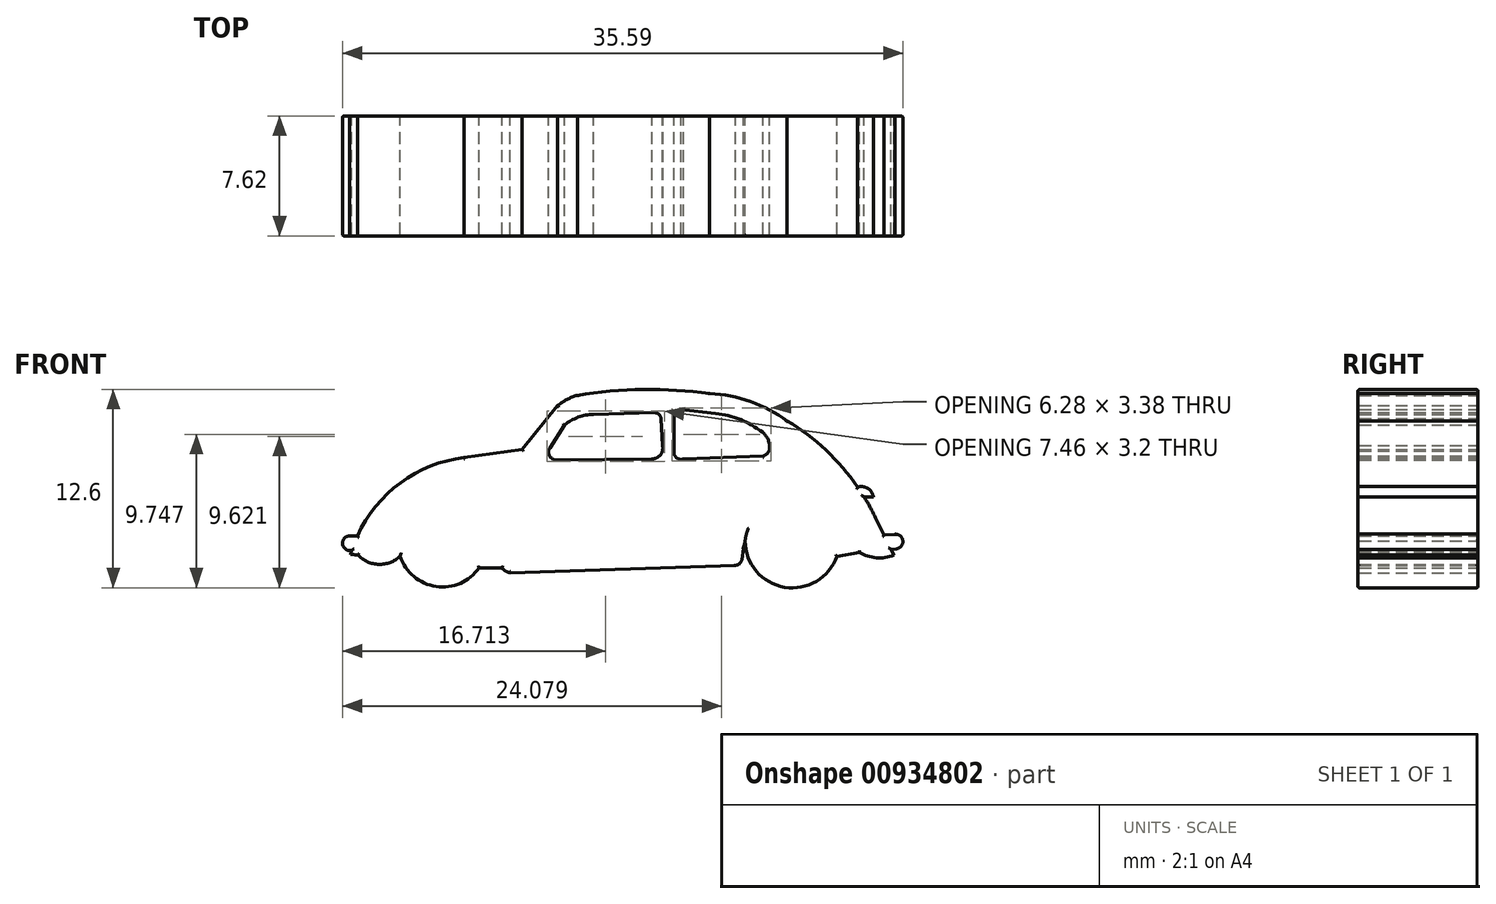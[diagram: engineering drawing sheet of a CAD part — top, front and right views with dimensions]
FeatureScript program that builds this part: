
annotation { "Feature Type Name" : "Feature", "Feature Type Description" : "" }
export const myFeature = defineFeature(function(context is Context, id is Id, definition is map)
    precondition{}
    {
        {
            var Q0;
            Q0=qCreatedBy(makeId("Front.planeOp"),FACE);
            var sketch = newSketch(context, id + "F0", { "sketchPlane" : qUnion([Q0])});
            skArc(sketch, "E0", {"start": v(-11.53, 23.27) * mm, "mid": v(-15.57, 21.68) * mm, "end": v(-18.3, 18.3) * mm});
            skArc(sketch, "E1", {"start": v(8.99, 25.61) * mm, "mid": v(6.65, 26.83) * mm, "end": v(4.07, 27.35) * mm});
            skArc(sketch, "E2", {"start": v(-15.59, 17) * mm, "mid": v(-13.3, 15.08) * mm, "end": v(-10.57, 16.27) * mm});
            skArc(sketch, "E3", {"start": v(6.32, 17.98) * mm, "mid": v(8.82, 15.04) * mm, "end": v(12.15, 17) * mm});
            skPoint(sketch, "E4.first.point", {"position": v(-9.3, 16.64) * mm});
            skPoint(sketch, "E4.second.point", {"position": v(-16.14, 17.08) * mm});
            skPoint(sketch, "E4.third.point", {"position": v(-15.9, 15.72) * mm});
            skPoint(sketch, "E5.first.point", {"position": v(6.84, 18.84) * mm});
            skPoint(sketch, "E5.second.point", {"position": v(12.55, 16.03) * mm});
            skPoint(sketch, "E5.third.point", {"position": v(9.32, 20.48) * mm});
            skLineSegment(sketch, "E6", {"start": v(-7.85, 23.8) * mm, "end": v(-5.6, 26.57) * mm});
            skLineSegment(sketch, "E7", {"start": v(-7.85, 23.8) * mm, "end": v(-11.53, 23.27) * mm});
            skPoint(sketch, "E8.second.point", {"position": v(-0.88, 20.92) * mm});
            skPoint(sketch, "E8.third.point", {"position": v(0.26, 22.68) * mm});
            skPoint(sketch, "E9.first.point", {"position": v(12.94, 17.76) * mm});
            skPoint(sketch, "E9.second.point", {"position": v(14.7, 18.65) * mm});
            skPoint(sketch, "E9.third.point", {"position": v(14.48, 18.97) * mm});
            skPoint(sketch, "E10.first.point", {"position": v(12.5, 18.64) * mm});
            skPoint(sketch, "E10.second.point", {"position": v(16.16, 21.44) * mm});
            skPoint(sketch, "E10.third.point", {"position": v(16.02, 21.52) * mm});
            skPoint(sketch, "E11.first.point", {"position": v(11.44, 23.75) * mm});
            skArc(sketch, "E12", {"start": v(-18.74, 17.14) * mm, "mid": v(-18.5, 17.1) * mm, "end": v(-18.27, 17.1) * mm});
            skPoint(sketch, "E12.first.point", {"position": v(-15.9, 18.25) * mm});
            skPoint(sketch, "E12.second.point", {"position": v(-20.76, 21.48) * mm});
            skPoint(sketch, "E12.third.point", {"position": v(-20.1, 17.77) * mm});
            skArc(sketch, "E13", {"start": v(-9.13, 16.27) * mm, "mid": v(-8.75, 16) * mm, "end": v(-8.27, 15.97) * mm});
            skPoint(sketch, "E13.second.point", {"position": v(-7.64, 17.02) * mm});
            skPoint(sketch, "E13.third.point", {"position": v(-8.6, 15.96) * mm});
            skLineSegment(sketch, "E14.trimOffspring", {"start": v(-8.6, 15.96) * mm, "end": v(-8.27, 15.97) * mm});
            skArc(sketch, "E15.trimOffspring", {"start": v(-4.34, 27.23) * mm, "mid": v(-5, 26.96) * mm, "end": v(-5.6, 26.57) * mm});
            skArc(sketch, "E16.trimOffspring", {"start": v(16.16, 21.44) * mm, "mid": v(16.09, 21.48) * mm, "end": v(16.02, 21.52) * mm});
            skArc(sketch, "E17.trimOffspring", {"start": v(14.61, 19.44) * mm, "mid": v(14.26, 20.12) * mm, "end": v(13.88, 20.77) * mm});
            skPoint(sketch, "E18.first.point", {"position": v(-9.43, 17.2) * mm});
            skPoint(sketch, "E18.second.point", {"position": v(-16.83, 16.34) * mm});
            skPoint(sketch, "E18.third.point", {"position": v(-14.78, 13.44) * mm});
            skArc(sketch, "E19", {"start": v(4.07, 27.35) * mm, "mid": v(-0.14, 27.6) * mm, "end": v(-4.34, 27.23) * mm});
            skPoint(sketch, "E20.end.orphan", {"position": v(4.07, 27.35) * mm});
            skArc(sketch, "E21", {"start": v(14.46, 20.77) * mm, "mid": v(14.1, 21.32) * mm, "end": v(13.47, 21.4) * mm});
            skPoint(sketch, "E21.first.point", {"position": v(13.47, 21.4) * mm});
            skPoint(sketch, "E21.second.point", {"position": v(13.78, 19.9) * mm});
            skPoint(sketch, "E21.third.point", {"position": v(14.26, 20.13) * mm});
            skLineSegment(sketch, "E22", {"start": v(14.46, 20.77) * mm, "end": v(13.88, 20.77) * mm});
            skArc(sketch, "E23.trimOffspring", {"start": v(13.47, 21.4) * mm, "mid": v(11.45, 23.74) * mm, "end": v(8.99, 25.61) * mm});
            skLineSegment(sketch, "E24", {"start": v(14.61, 19.44) * mm, "end": v(15.14, 18.36) * mm});
            skArc(sketch, "E25", {"start": v(15.9, 17.47) * mm, "mid": v(16.34, 17.97) * mm, "end": v(15.83, 18.4) * mm});
            skLineSegment(sketch, "E26", {"start": v(15.9, 17.47) * mm, "end": v(15.59, 17.45) * mm});
            skLineSegment(sketch, "E27", {"start": v(15.83, 18.4) * mm, "end": v(15.14, 18.36) * mm});
            skPoint(sketch, "E27.endSnap0", {"position": v(15.2, 18.26) * mm});
            skPoint(sketch, "E28.orphan", {"position": v(15.2, 18.36) * mm});
            skArc(sketch, "E29", {"start": v(-18.76, 18.3) * mm, "mid": v(-19.25, 17.87) * mm, "end": v(-18.83, 17.37) * mm});
            skArc(sketch, "E30.trimOffspring", {"start": v(-18.67, 17.37) * mm, "mid": v(-18.7, 17.25) * mm, "end": v(-18.74, 17.14) * mm});
            skLineSegment(sketch, "E31", {"start": v(-18.8, 18.3) * mm, "end": v(-18.3, 18.3) * mm});
            skLineSegment(sketch, "E32", {"start": v(-18.83, 17.37) * mm, "end": v(-18.67, 17.37) * mm});
            skPoint(sketch, "E33.orphan", {"position": v(-18.3, 17.38) * mm});
            skPoint(sketch, "E34.orphan", {"position": v(-18.66, 17.38) * mm});
            skLineSegment(sketch, "E35.trimOffspring", {"start": v(15.59, 17.45) * mm, "end": v(15.77, 17.08) * mm});
            skPoint(sketch, "E36.first.point", {"position": v(7.3, 19.61) * mm});
            skPoint(sketch, "E36.second.point", {"position": v(11.9, 14.6) * mm});
            skPoint(sketch, "E36.third.point", {"position": v(12.82, 16.03) * mm});
            skArc(sketch, "E37", {"start": v(5.67, 16.42) * mm, "mid": v(5.96, 16.53) * mm, "end": v(6.12, 16.8) * mm});
            skPoint(sketch, "E37.first.point", {"position": v(6.12, 16.93) * mm});
            skPoint(sketch, "E37.second.point", {"position": v(5.22, 16.82) * mm});
            skPoint(sketch, "E37.third.point", {"position": v(5.67, 16.42) * mm});
            skLineSegment(sketch, "E38", {"start": v(6.23, 17.51) * mm, "end": v(6.12, 16.8) * mm});
            skArc(sketch, "E39.trimOffspring", {"start": v(6.32, 17.98) * mm, "mid": v(6.27, 17.75) * mm, "end": v(6.23, 17.51) * mm});
            skPoint(sketch, "E40.first.point", {"position": v(0.33, 26.04) * mm});
            skPoint(sketch, "E40.second.point", {"position": v(0.73, 25.33) * mm});
            skPoint(sketch, "E40.third.point", {"position": v(0.53, 25.3) * mm});
            skArc(sketch, "E41", {"start": v(0.4, 23.19) * mm, "mid": v(0.94, 23.44) * mm, "end": v(1.07, 24.03) * mm});
            skPoint(sketch, "E41.first.point", {"position": v(1.07, 23.71) * mm});
            skPoint(sketch, "E41.second.point", {"position": v(-0.24, 24.08) * mm});
            skPoint(sketch, "E41.third.point", {"position": v(0.4, 23.19) * mm});
            skArc(sketch, "E42", {"start": v(-6.05, 23.94) * mm, "mid": v(-6.11, 23.4) * mm, "end": v(-5.64, 23.12) * mm});
            skPoint(sketch, "E42.first.point", {"position": v(-5.92, 23.19) * mm});
            skPoint(sketch, "E42.second.point", {"position": v(-5.35, 24) * mm});
            skPoint(sketch, "E42.third.point", {"position": v(-5.6, 24.12) * mm});
            skArc(sketch, "E43", {"start": v(-3.31, 26.01) * mm, "mid": v(-4.29, 25.83) * mm, "end": v(-5.15, 25.33) * mm});
            skPoint(sketch, "E43.first.point", {"position": v(-5.15, 25.33) * mm});
            skPoint(sketch, "E43.second.point", {"position": v(-1.4, 21) * mm});
            skPoint(sketch, "E43.third.point", {"position": v(-0.47, 23.64) * mm});
            skLineSegment(sketch, "E44", {"start": v(-5.15, 25.33) * mm, "end": v(-6.08, 23.9) * mm});
            skLineSegment(sketch, "E45", {"start": v(-3.31, 26.01) * mm, "end": v(0.56, 26.12) * mm});
            skLineSegment(sketch, "E46", {"start": v(-5.64, 23.12) * mm, "end": v(0.4, 23.19) * mm});
            skLineSegment(sketch, "E47", {"start": v(1.07, 24.03) * mm, "end": v(0.98, 25.73) * mm});
            skArc(sketch, "E48.trimOffspring", {"start": v(0.98, 25.73) * mm, "mid": v(0.75, 26.08) * mm, "end": v(0.33, 26.04) * mm});
            skArc(sketch, "E49.trimOffspring", {"start": v(-6.05, 23.95) * mm, "mid": v(-6.05, 23.95) * mm, "end": v(-6.05, 23.94) * mm});
            skArc(sketch, "E50", {"start": v(2.25, 26.33) * mm, "mid": v(1.9, 26.13) * mm, "end": v(1.79, 25.75) * mm});
            skPoint(sketch, "E50.first.point", {"position": v(1.79, 25.85) * mm});
            skPoint(sketch, "E50.second.point", {"position": v(2.85, 25.68) * mm});
            skPoint(sketch, "E50.third.point", {"position": v(2.05, 25.34) * mm});
            skArc(sketch, "E51", {"start": v(1.8, 23.68) * mm, "mid": v(1.96, 23.26) * mm, "end": v(2.41, 23.19) * mm});
            skPoint(sketch, "E51.first.point", {"position": v(1.8, 23.68) * mm});
            skPoint(sketch, "E51.second.point", {"position": v(2.7, 23.57) * mm});
            skPoint(sketch, "E51.third.point", {"position": v(2.7, 23.72) * mm});
            skPoint(sketch, "E52.first.point", {"position": v(7.78, 23.5) * mm});
            skPoint(sketch, "E52.second.point", {"position": v(5.63, 24.43) * mm});
            skPoint(sketch, "E52.third.point", {"position": v(5.78, 23.24) * mm});
            skArc(sketch, "E53", {"start": v(1.79, 25.8) * mm, "mid": v(1.79, 25.8) * mm, "end": v(1.79, 25.8) * mm});
            skPoint(sketch, "E53.first.point", {"position": v(7.41, 24.88) * mm});
            skPoint(sketch, "E53.second.point", {"position": v(-0.05, 15.42) * mm});
            skPoint(sketch, "E53.third.point", {"position": v(3.06, 26.08) * mm});
            skArc(sketch, "E54", {"start": v(7.46, 23.38) * mm, "mid": v(7.7, 23.51) * mm, "end": v(7.85, 23.74) * mm});
            skPoint(sketch, "E54.first.point", {"position": v(7.46, 23.38) * mm});
            skPoint(sketch, "E54.second.point", {"position": v(7.16, 24.47) * mm});
            skPoint(sketch, "E54.third.point", {"position": v(7.12, 24.46) * mm});
            skLineSegment(sketch, "E55", {"start": v(2.41, 23.19) * mm, "end": v(7.46, 23.38) * mm});
            skLineSegment(sketch, "E56", {"start": v(2.25, 26.33) * mm, "end": v(4.45, 26.08) * mm});
            skLineSegment(sketch, "E57", {"start": v(1.79, 25.85) * mm, "end": v(1.8, 23.68) * mm});
            skArc(sketch, "E58.trimOffspring", {"start": v(7.85, 23.74) * mm, "mid": v(7.8, 24.38) * mm, "end": v(7.41, 24.88) * mm});
            skArc(sketch, "E59.trimOffspring", {"start": v(7.41, 24.88) * mm, "mid": v(6, 25.68) * mm, "end": v(4.45, 26.08) * mm});
            skPoint(sketch, "E60.first.point", {"position": v(-17.23, 16.52) * mm});
            skPoint(sketch, "E60.second.point", {"position": v(-16.33, 20.19) * mm});
            skPoint(sketch, "E60.third.point", {"position": v(-16.6, 20.25) * mm});
            skArc(sketch, "E61.trimOffspring", {"start": v(-18.27, 17.1) * mm, "mid": v(-16.95, 16.5) * mm, "end": v(-15.59, 17) * mm});
            skLineSegment(sketch, "E62", {"start": v(-10.57, 16.27) * mm, "end": v(-9.13, 16.27) * mm});
            skLineSegment(sketch, "E63", {"start": v(12.15, 17) * mm, "end": v(13.57, 17.26) * mm});
            skArc(sketch, "E64.trimOffspring", {"start": v(13.57, 17.26) * mm, "mid": v(14.65, 16.9) * mm, "end": v(15.77, 17.08) * mm});
            skPoint(sketch, "E65.1.36", {"position": v(-25.13, -61.05) * mm});
            skPoint(sketch, "E66", {"position": v(-1.45, 16.2) * mm});
            skLineSegment(sketch, "E67", {"start": v(-8.6, 15.96) * mm, "end": v(5.7, 16.43) * mm});
            skPoint(sketch, "E68", {"position": v(-5.03, 16.07) * mm});
            skPoint(sketch, "E69", {"position": v(2.12, 16.3) * mm});
            skSolve(sketch);
        }
        {
            var Q0;
            {var subQ37=sQuery(id+"F0.wireOp",EDGE,"E0");Q0=makeQuery(id+"F0.imprint","IMPRINT",FACE,{"disambiguationData":[TD([[makeQuery(id+"F0.imprint","IMPRINT",EDGE,{"derivedFrom":subQ37}),1.0]])]});}
            extrude(context, id + "F1", {"entities" : qUnion([Q0]), "depth" : 7.62 * mm, "offsetDistance" : 25 * mm});
        }
        {
            var Q0;
            Q0=makeQuery(id+"F1.opExtrude","CAP_FACE",FACE,{"disambiguationData":[OSD([sQuery(id+"F0.wireOp",EDGE,"E0"),sQuery(id+"F0.wireOp",EDGE,"E1"),sQuery(id+"F0.wireOp",EDGE,"E2"),sQuery(id+"F0.wireOp",EDGE,"E3"),sQuery(id+"F0.wireOp",EDGE,"E6"),sQuery(id+"F0.wireOp",EDGE,"E7"),sQuery(id+"F0.wireOp",EDGE,"E12"),sQuery(id+"F0.wireOp",EDGE,"E13"),sQuery(id+"F0.wireOp",EDGE,"E15.trimOffspring"),sQuery(id+"F0.wireOp",EDGE,"E17.trimOffspring"),sQuery(id+"F0.wireOp",EDGE,"E19"),sQuery(id+"F0.wireOp",EDGE,"E21"),sQuery(id+"F0.wireOp",EDGE,"E22"),sQuery(id+"F0.wireOp",EDGE,"E23.trimOffspring"),sQuery(id+"F0.wireOp",EDGE,"E24"),sQuery(id+"F0.wireOp",EDGE,"E25"),sQuery(id+"F0.wireOp",EDGE,"E26"),sQuery(id+"F0.wireOp",EDGE,"E27"),sQuery(id+"F0.wireOp",EDGE,"E29"),sQuery(id+"F0.wireOp",EDGE,"E30.trimOffspring"),sQuery(id+"F0.wireOp",EDGE,"E31"),sQuery(id+"F0.wireOp",EDGE,"E32"),sQuery(id+"F0.wireOp",EDGE,"E35.trimOffspring"),sQuery(id+"F0.wireOp",EDGE,"E37"),sQuery(id+"F0.wireOp",EDGE,"E38"),sQuery(id+"F0.wireOp",EDGE,"E39.trimOffspring"),sQuery(id+"F0.wireOp",EDGE,"E41"),sQuery(id+"F0.wireOp",EDGE,"E42"),sQuery(id+"F0.wireOp",EDGE,"E43"),sQuery(id+"F0.wireOp",EDGE,"E44"),sQuery(id+"F0.wireOp",EDGE,"E45"),sQuery(id+"F0.wireOp",EDGE,"E46"),sQuery(id+"F0.wireOp",EDGE,"E47"),sQuery(id+"F0.wireOp",EDGE,"E48.trimOffspring"),sQuery(id+"F0.wireOp",EDGE,"E50"),sQuery(id+"F0.wireOp",EDGE,"E51"),sQuery(id+"F0.wireOp",EDGE,"E54"),sQuery(id+"F0.wireOp",EDGE,"E55"),sQuery(id+"F0.wireOp",EDGE,"E56"),sQuery(id+"F0.wireOp",EDGE,"E57"),sQuery(id+"F0.wireOp",EDGE,"E58.trimOffspring"),sQuery(id+"F0.wireOp",EDGE,"E59.trimOffspring"),sQuery(id+"F0.wireOp",EDGE,"E61.trimOffspring"),sQuery(id+"F0.wireOp",EDGE,"E62"),sQuery(id+"F0.wireOp",EDGE,"E63"),sQuery(id+"F0.wireOp",EDGE,"E64.trimOffspring"),sQuery(id+"F0.wireOp",EDGE,"E65.1.40"),sQuery(id+"F0.wireOp",EDGE,"E65.1.43"),sQuery(id+"F0.wireOp",EDGE,"E65.1.65"),sQuery(id+"F0.wireOp",EDGE,"E65.1.67"),sQuery(id+"F0.wireOp",EDGE,"E65.1.70"),sQuery(id+"F0.wireOp",EDGE,"E65.1.75"),sQuery(id+"F0.wireOp",EDGE,"E65.1.76"),sQuery(id+"F0.wireOp",EDGE,"E65.1.77"),sQuery(id+"F0.wireOp",EDGE,"E65.1.78"),sQuery(id+"F0.wireOp",EDGE,"E65.1.79"),sQuery(id+"F0.wireOp",EDGE,"E65.1.80"),sQuery(id+"F0.wireOp",EDGE,"E65.1.81"),sQuery(id+"F0.wireOp",EDGE,"E65.1.82"),sQuery(id+"F0.wireOp",EDGE,"E65.1.84"),sQuery(id+"F0.wireOp",EDGE,"E65.1.85"),sQuery(id+"F0.wireOp",EDGE,"E65.1.86"),sQuery(id+"F0.wireOp",EDGE,"E65.1.87"),sQuery(id+"F0.wireOp",EDGE,"E65.1.88"),sQuery(id+"F0.wireOp",EDGE,"E65.1.89"),sQuery(id+"F0.wireOp",EDGE,"E65.1.90"),sQuery(id+"F0.wireOp",EDGE,"E65.1.91"),sQuery(id+"F0.wireOp",EDGE,"E65.1.92"),sQuery(id+"F0.wireOp",EDGE,"E65.1.93"),sQuery(id+"F0.wireOp",EDGE,"E65.1.94"),sQuery(id+"F0.wireOp",EDGE,"E65.1.95"),sQuery(id+"F0.wireOp",EDGE,"E65.1.96"),sQuery(id+"F0.wireOp",EDGE,"E65.1.97"),sQuery(id+"F0.wireOp",EDGE,"E65.1.99"),sQuery(id+"F0.wireOp",EDGE,"E65.1.100"),sQuery(id+"F0.wireOp",EDGE,"E65.1.101"),sQuery(id+"F0.wireOp",EDGE,"E65.1.102"),sQuery(id+"F0.wireOp",EDGE,"E65.1.103"),sQuery(id+"F0.wireOp",EDGE,"E65.1.105"),sQuery(id+"F0.wireOp",EDGE,"E65.1.106"),sQuery(id+"F0.wireOp",EDGE,"E65.1.107"),sQuery(id+"F0.wireOp",EDGE,"E65.1.108"),sQuery(id+"F0.wireOp",EDGE,"E65.1.109"),sQuery(id+"F0.wireOp",EDGE,"E65.1.110"),sQuery(id+"F0.wireOp",EDGE,"E65.1.111"),sQuery(id+"F0.wireOp",EDGE,"E65.1.112"),sQuery(id+"F0.wireOp",EDGE,"E65.1.113"),sQuery(id+"F0.wireOp",EDGE,"E65.1.114"),sQuery(id+"F0.wireOp",EDGE,"E65.1.116"),sQuery(id+"F0.wireOp",EDGE,"E65.1.117"),sQuery(id+"F0.wireOp",EDGE,"E65.1.118"),sQuery(id+"F0.wireOp",EDGE,"E65.1.119"),sQuery(id+"F0.wireOp",EDGE,"E65.1.120"),sQuery(id+"F0.wireOp",EDGE,"E65.2.40"),sQuery(id+"F0.wireOp",EDGE,"E65.2.43"),sQuery(id+"F0.wireOp",EDGE,"E65.2.65"),sQuery(id+"F0.wireOp",EDGE,"E65.2.67"),sQuery(id+"F0.wireOp",EDGE,"E65.2.70"),sQuery(id+"F0.wireOp",EDGE,"E65.2.75"),sQuery(id+"F0.wireOp",EDGE,"E65.2.76"),sQuery(id+"F0.wireOp",EDGE,"E65.2.77"),sQuery(id+"F0.wireOp",EDGE,"E65.2.78"),sQuery(id+"F0.wireOp",EDGE,"E65.2.79"),sQuery(id+"F0.wireOp",EDGE,"E65.2.80"),sQuery(id+"F0.wireOp",EDGE,"E65.2.81"),sQuery(id+"F0.wireOp",EDGE,"E65.2.82"),sQuery(id+"F0.wireOp",EDGE,"E65.2.84"),sQuery(id+"F0.wireOp",EDGE,"E65.2.85"),sQuery(id+"F0.wireOp",EDGE,"E65.2.86"),sQuery(id+"F0.wireOp",EDGE,"E65.2.87"),sQuery(id+"F0.wireOp",EDGE,"E65.2.88"),sQuery(id+"F0.wireOp",EDGE,"E65.2.89"),sQuery(id+"F0.wireOp",EDGE,"E65.2.90"),sQuery(id+"F0.wireOp",EDGE,"E65.2.91"),sQuery(id+"F0.wireOp",EDGE,"E65.2.92"),sQuery(id+"F0.wireOp",EDGE,"E65.2.93"),sQuery(id+"F0.wireOp",EDGE,"E65.2.94"),sQuery(id+"F0.wireOp",EDGE,"E65.2.95"),sQuery(id+"F0.wireOp",EDGE,"E65.2.96"),sQuery(id+"F0.wireOp",EDGE,"E65.2.97"),sQuery(id+"F0.wireOp",EDGE,"E65.2.99"),sQuery(id+"F0.wireOp",EDGE,"E65.2.100"),sQuery(id+"F0.wireOp",EDGE,"E65.2.101"),sQuery(id+"F0.wireOp",EDGE,"E65.2.102"),sQuery(id+"F0.wireOp",EDGE,"E65.2.103"),sQuery(id+"F0.wireOp",EDGE,"E65.2.105"),sQuery(id+"F0.wireOp",EDGE,"E65.2.106"),sQuery(id+"F0.wireOp",EDGE,"E65.2.107"),sQuery(id+"F0.wireOp",EDGE,"E65.2.108"),sQuery(id+"F0.wireOp",EDGE,"E65.2.109"),sQuery(id+"F0.wireOp",EDGE,"E65.2.110"),sQuery(id+"F0.wireOp",EDGE,"E65.2.111"),sQuery(id+"F0.wireOp",EDGE,"E65.2.112"),sQuery(id+"F0.wireOp",EDGE,"E65.2.113"),sQuery(id+"F0.wireOp",EDGE,"E65.2.114"),sQuery(id+"F0.wireOp",EDGE,"E65.2.116"),sQuery(id+"F0.wireOp",EDGE,"E65.2.117"),sQuery(id+"F0.wireOp",EDGE,"E65.2.118"),sQuery(id+"F0.wireOp",EDGE,"E65.2.119"),sQuery(id+"F0.wireOp",EDGE,"E65.2.120"),sQuery(id+"F0.wireOp",EDGE,"cX2E59e6-YhH1-Q1MG-Sjdk-BAABhza4ufgR"),sQuery(id+"F0.wireOp",EDGE,"E67"),sQuery(id+"F0.wireOp",EDGE,"66dcf0ee-2a08-4a9d-b759-8287c14c5916.trimOffspring"),sQuery(id+"F0.wireOp",EDGE,"a76f836b-d861-43b1-a47d-e243f5533e53.0"),sQuery(id+"F0.wireOp",EDGE,"7d4328b9-f5d3-4442-a268-a991dec6ba42.trimOffspring"),sQuery(id+"F0.wireOp",EDGE,"2053e8fe-d855-4237-9356-6a511fd7d272.trimOffspring"),sQuery(id+"F0.wireOp",EDGE,"f4915061-0bcc-4255-bb53-9f7686e6b51c.1.0"),sQuery(id+"F0.wireOp",EDGE,"f4915061-0bcc-4255-bb53-9f7686e6b51c.1.1"),sQuery(id+"F0.wireOp",EDGE,"f4915061-0bcc-4255-bb53-9f7686e6b51c.2.0"),sQuery(id+"F0.wireOp",EDGE,"f4915061-0bcc-4255-bb53-9f7686e6b51c.2.1"),sQuery(id+"F0.wireOp",EDGE,"3bdfe863-bdbf-45cc-8d97-358fdc77690e.trimOffspring"),sQuery(id+"F0.wireOp",EDGE,"17896dc9-20ad-4a46-b1d6-c86808146626.trimOffspring"),sQuery(id+"F0.wireOp",EDGE,"197432aa-425d-4298-81c5-e785456323d7.trimOffspring"),sQuery(id+"F0.wireOp",EDGE,"66babc20-0dfa-44de-9627-1df3a82dac77.trimOffspring")])],"isStart":false});
            var Q1;
            Q1=makeQuery(id+"F1.opExtrude","CAP_FACE",FACE,{"disambiguationData":[OSD([sQuery(id+"F0.wireOp",EDGE,"E0"),sQuery(id+"F0.wireOp",EDGE,"E1"),sQuery(id+"F0.wireOp",EDGE,"E2"),sQuery(id+"F0.wireOp",EDGE,"E3"),sQuery(id+"F0.wireOp",EDGE,"E6"),sQuery(id+"F0.wireOp",EDGE,"E7"),sQuery(id+"F0.wireOp",EDGE,"E12"),sQuery(id+"F0.wireOp",EDGE,"E13"),sQuery(id+"F0.wireOp",EDGE,"E15.trimOffspring"),sQuery(id+"F0.wireOp",EDGE,"E17.trimOffspring"),sQuery(id+"F0.wireOp",EDGE,"E19"),sQuery(id+"F0.wireOp",EDGE,"E21"),sQuery(id+"F0.wireOp",EDGE,"E22"),sQuery(id+"F0.wireOp",EDGE,"E23.trimOffspring"),sQuery(id+"F0.wireOp",EDGE,"E24"),sQuery(id+"F0.wireOp",EDGE,"E25"),sQuery(id+"F0.wireOp",EDGE,"E26"),sQuery(id+"F0.wireOp",EDGE,"E27"),sQuery(id+"F0.wireOp",EDGE,"E29"),sQuery(id+"F0.wireOp",EDGE,"E30.trimOffspring"),sQuery(id+"F0.wireOp",EDGE,"E31"),sQuery(id+"F0.wireOp",EDGE,"E32"),sQuery(id+"F0.wireOp",EDGE,"E35.trimOffspring"),sQuery(id+"F0.wireOp",EDGE,"E37"),sQuery(id+"F0.wireOp",EDGE,"E38"),sQuery(id+"F0.wireOp",EDGE,"E39.trimOffspring"),sQuery(id+"F0.wireOp",EDGE,"E41"),sQuery(id+"F0.wireOp",EDGE,"E42"),sQuery(id+"F0.wireOp",EDGE,"E43"),sQuery(id+"F0.wireOp",EDGE,"E44"),sQuery(id+"F0.wireOp",EDGE,"E45"),sQuery(id+"F0.wireOp",EDGE,"E46"),sQuery(id+"F0.wireOp",EDGE,"E47"),sQuery(id+"F0.wireOp",EDGE,"E48.trimOffspring"),sQuery(id+"F0.wireOp",EDGE,"E50"),sQuery(id+"F0.wireOp",EDGE,"E51"),sQuery(id+"F0.wireOp",EDGE,"E54"),sQuery(id+"F0.wireOp",EDGE,"E55"),sQuery(id+"F0.wireOp",EDGE,"E56"),sQuery(id+"F0.wireOp",EDGE,"E57"),sQuery(id+"F0.wireOp",EDGE,"E58.trimOffspring"),sQuery(id+"F0.wireOp",EDGE,"E59.trimOffspring"),sQuery(id+"F0.wireOp",EDGE,"E61.trimOffspring"),sQuery(id+"F0.wireOp",EDGE,"E62"),sQuery(id+"F0.wireOp",EDGE,"E63"),sQuery(id+"F0.wireOp",EDGE,"E64.trimOffspring"),sQuery(id+"F0.wireOp",EDGE,"E65.1.40"),sQuery(id+"F0.wireOp",EDGE,"E65.1.43"),sQuery(id+"F0.wireOp",EDGE,"E65.1.65"),sQuery(id+"F0.wireOp",EDGE,"E65.1.67"),sQuery(id+"F0.wireOp",EDGE,"E65.1.70"),sQuery(id+"F0.wireOp",EDGE,"E65.1.75"),sQuery(id+"F0.wireOp",EDGE,"E65.1.76"),sQuery(id+"F0.wireOp",EDGE,"E65.1.77"),sQuery(id+"F0.wireOp",EDGE,"E65.1.78"),sQuery(id+"F0.wireOp",EDGE,"E65.1.79"),sQuery(id+"F0.wireOp",EDGE,"E65.1.80"),sQuery(id+"F0.wireOp",EDGE,"E65.1.81"),sQuery(id+"F0.wireOp",EDGE,"E65.1.82"),sQuery(id+"F0.wireOp",EDGE,"E65.1.84"),sQuery(id+"F0.wireOp",EDGE,"E65.1.85"),sQuery(id+"F0.wireOp",EDGE,"E65.1.86"),sQuery(id+"F0.wireOp",EDGE,"E65.1.87"),sQuery(id+"F0.wireOp",EDGE,"E65.1.88"),sQuery(id+"F0.wireOp",EDGE,"E65.1.89"),sQuery(id+"F0.wireOp",EDGE,"E65.1.90"),sQuery(id+"F0.wireOp",EDGE,"E65.1.91"),sQuery(id+"F0.wireOp",EDGE,"E65.1.92"),sQuery(id+"F0.wireOp",EDGE,"E65.1.93"),sQuery(id+"F0.wireOp",EDGE,"E65.1.94"),sQuery(id+"F0.wireOp",EDGE,"E65.1.95"),sQuery(id+"F0.wireOp",EDGE,"E65.1.96"),sQuery(id+"F0.wireOp",EDGE,"E65.1.97"),sQuery(id+"F0.wireOp",EDGE,"E65.1.99"),sQuery(id+"F0.wireOp",EDGE,"E65.1.100"),sQuery(id+"F0.wireOp",EDGE,"E65.1.101"),sQuery(id+"F0.wireOp",EDGE,"E65.1.102"),sQuery(id+"F0.wireOp",EDGE,"E65.1.103"),sQuery(id+"F0.wireOp",EDGE,"E65.1.105"),sQuery(id+"F0.wireOp",EDGE,"E65.1.106"),sQuery(id+"F0.wireOp",EDGE,"E65.1.107"),sQuery(id+"F0.wireOp",EDGE,"E65.1.108"),sQuery(id+"F0.wireOp",EDGE,"E65.1.109"),sQuery(id+"F0.wireOp",EDGE,"E65.1.110"),sQuery(id+"F0.wireOp",EDGE,"E65.1.111"),sQuery(id+"F0.wireOp",EDGE,"E65.1.112"),sQuery(id+"F0.wireOp",EDGE,"E65.1.113"),sQuery(id+"F0.wireOp",EDGE,"E65.1.114"),sQuery(id+"F0.wireOp",EDGE,"E65.1.116"),sQuery(id+"F0.wireOp",EDGE,"E65.1.117"),sQuery(id+"F0.wireOp",EDGE,"E65.1.118"),sQuery(id+"F0.wireOp",EDGE,"E65.1.119"),sQuery(id+"F0.wireOp",EDGE,"E65.1.120"),sQuery(id+"F0.wireOp",EDGE,"E65.2.40"),sQuery(id+"F0.wireOp",EDGE,"E65.2.43"),sQuery(id+"F0.wireOp",EDGE,"E65.2.65"),sQuery(id+"F0.wireOp",EDGE,"E65.2.67"),sQuery(id+"F0.wireOp",EDGE,"E65.2.70"),sQuery(id+"F0.wireOp",EDGE,"E65.2.75"),sQuery(id+"F0.wireOp",EDGE,"E65.2.76"),sQuery(id+"F0.wireOp",EDGE,"E65.2.77"),sQuery(id+"F0.wireOp",EDGE,"E65.2.78"),sQuery(id+"F0.wireOp",EDGE,"E65.2.79"),sQuery(id+"F0.wireOp",EDGE,"E65.2.80"),sQuery(id+"F0.wireOp",EDGE,"E65.2.81"),sQuery(id+"F0.wireOp",EDGE,"E65.2.82"),sQuery(id+"F0.wireOp",EDGE,"E65.2.84"),sQuery(id+"F0.wireOp",EDGE,"E65.2.85"),sQuery(id+"F0.wireOp",EDGE,"E65.2.86"),sQuery(id+"F0.wireOp",EDGE,"E65.2.87"),sQuery(id+"F0.wireOp",EDGE,"E65.2.88"),sQuery(id+"F0.wireOp",EDGE,"E65.2.89"),sQuery(id+"F0.wireOp",EDGE,"E65.2.90"),sQuery(id+"F0.wireOp",EDGE,"E65.2.91"),sQuery(id+"F0.wireOp",EDGE,"E65.2.92"),sQuery(id+"F0.wireOp",EDGE,"E65.2.93"),sQuery(id+"F0.wireOp",EDGE,"E65.2.94"),sQuery(id+"F0.wireOp",EDGE,"E65.2.95"),sQuery(id+"F0.wireOp",EDGE,"E65.2.96"),sQuery(id+"F0.wireOp",EDGE,"E65.2.97"),sQuery(id+"F0.wireOp",EDGE,"E65.2.99"),sQuery(id+"F0.wireOp",EDGE,"E65.2.100"),sQuery(id+"F0.wireOp",EDGE,"E65.2.101"),sQuery(id+"F0.wireOp",EDGE,"E65.2.102"),sQuery(id+"F0.wireOp",EDGE,"E65.2.103"),sQuery(id+"F0.wireOp",EDGE,"E65.2.105"),sQuery(id+"F0.wireOp",EDGE,"E65.2.106"),sQuery(id+"F0.wireOp",EDGE,"E65.2.107"),sQuery(id+"F0.wireOp",EDGE,"E65.2.108"),sQuery(id+"F0.wireOp",EDGE,"E65.2.109"),sQuery(id+"F0.wireOp",EDGE,"E65.2.110"),sQuery(id+"F0.wireOp",EDGE,"E65.2.111"),sQuery(id+"F0.wireOp",EDGE,"E65.2.112"),sQuery(id+"F0.wireOp",EDGE,"E65.2.113"),sQuery(id+"F0.wireOp",EDGE,"E65.2.114"),sQuery(id+"F0.wireOp",EDGE,"E65.2.116"),sQuery(id+"F0.wireOp",EDGE,"E65.2.117"),sQuery(id+"F0.wireOp",EDGE,"E65.2.118"),sQuery(id+"F0.wireOp",EDGE,"E65.2.119"),sQuery(id+"F0.wireOp",EDGE,"E65.2.120"),sQuery(id+"F0.wireOp",EDGE,"cX2E59e6-YhH1-Q1MG-Sjdk-BAABhza4ufgR"),sQuery(id+"F0.wireOp",EDGE,"E67"),sQuery(id+"F0.wireOp",EDGE,"66dcf0ee-2a08-4a9d-b759-8287c14c5916.trimOffspring"),sQuery(id+"F0.wireOp",EDGE,"a76f836b-d861-43b1-a47d-e243f5533e53.0"),sQuery(id+"F0.wireOp",EDGE,"7d4328b9-f5d3-4442-a268-a991dec6ba42.trimOffspring"),sQuery(id+"F0.wireOp",EDGE,"2053e8fe-d855-4237-9356-6a511fd7d272.trimOffspring"),sQuery(id+"F0.wireOp",EDGE,"f4915061-0bcc-4255-bb53-9f7686e6b51c.1.0"),sQuery(id+"F0.wireOp",EDGE,"f4915061-0bcc-4255-bb53-9f7686e6b51c.1.1"),sQuery(id+"F0.wireOp",EDGE,"f4915061-0bcc-4255-bb53-9f7686e6b51c.2.0"),sQuery(id+"F0.wireOp",EDGE,"f4915061-0bcc-4255-bb53-9f7686e6b51c.2.1"),sQuery(id+"F0.wireOp",EDGE,"3bdfe863-bdbf-45cc-8d97-358fdc77690e.trimOffspring"),sQuery(id+"F0.wireOp",EDGE,"17896dc9-20ad-4a46-b1d6-c86808146626.trimOffspring"),sQuery(id+"F0.wireOp",EDGE,"197432aa-425d-4298-81c5-e785456323d7.trimOffspring"),sQuery(id+"F0.wireOp",EDGE,"66babc20-0dfa-44de-9627-1df3a82dac77.trimOffspring")])],"isStart":true});
            fillet(context, id + "F2", {"entities" : qUnion([Q0, Q1]), "radius" : .1 * mm, "tangentPropagation" : true, "allowEdgeOverflow" : false});
        }
    });
